# Revit family: KKDC_TiMi-C_kR207_3000K_1000mm
name_source: partatom
category: 조명 설비
units: mm (PartAtom-declared; Revit-internal decimal feet)

## family parameters
OmniClass 번호 = 23.80.70.11.14.17
OmniClass 제목 = Direct/Indirect
공유 = 아니오
광원 = 예
로드될 때 보이드를 사용하여 절단 = 아니오
룸 계산 점 = 아니오
부품 유형 = 배선함
원형 커넥터 치수 = 지름 사용
작업 기준면 기반 = 아니오
주석 방향 유지 = 아니오
항상 수직 = 예

## types (2) — shared parameters
Height = 12  [stored 0.0393701 ft]
Length = 1000  [stored 3.28084 ft]
Width = 15  [stored 0.0492126 ft]
감광 램프 색상 온도 변화 = <없음>
경사도 = 90.00°
렌더링 시 발산 모양 표시 = 예
색상 필터 = 16777215
직사각형 길이에서 발산 = 15  [stored 0.0492126 ft]
직사각형 폭에서 발산 = 1000  [stored 3.28084 ft]
zero-valued in all types: 기본 높이

## per-type parameters (varying)
| type | 램프 | 와티지 해설 | 측광 웹 파일 |
| TiMi-C kR207 2100K + 5000K Clear cover 1000mm | kR020 | 20W/m | TiMi-C Clear Cover R207(K-line).IES |
| TiMi-C kR207 2100K + 5000K Diffused cover 1000mm | kR207 | 16W/m | TiMi-C Diffused Cover R207(K-line).IES |

note: [stored X ft] marks values corroborated as IEEE doubles in the binary element streams (Revit-internal decimal feet)
